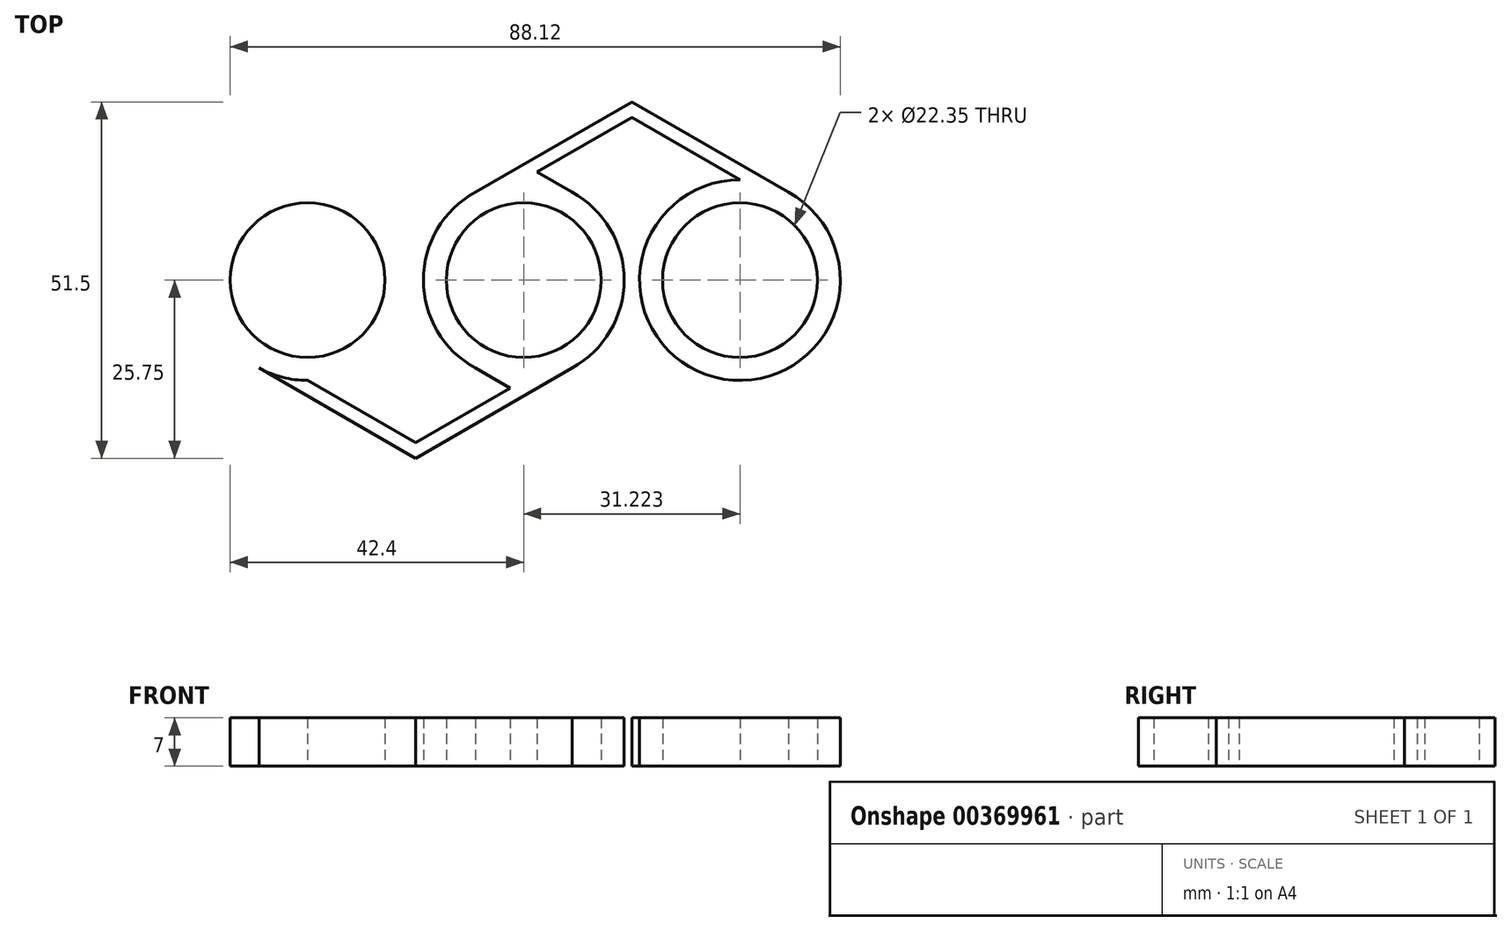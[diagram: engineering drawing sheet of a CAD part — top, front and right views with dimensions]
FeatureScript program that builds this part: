
annotation { "Feature Type Name" : "Feature", "Feature Type Description" : "" }
export const myFeature = defineFeature(function(context is Context, id is Id, definition is map)
    precondition{}
    {
        {
            var Q0;
            Q0=qCreatedBy(makeId("Top.planeOp"),FACE);
            var sketch = newSketch(context, id + "F0", { "sketchPlane" : qUnion([Q0])});
            skCircle(sketch, "E0", {"center": v(0, 0) * mm, "radius": 11.18 * mm});
            skCircle(sketch, "E1", {"center": v(0, 0) * mm, "radius": 14.5 * mm});
            skCircle(sketch, "E2", {"center": v(-31.22, 0) * mm, "radius": 11.18 * mm});
            skCircle(sketch, "E3", {"center": v(-31.22, 0) * mm, "radius": 14.5 * mm});
            skLineSegment(sketch, "E4", {"start": v(-31.22, 0) * mm, "end": v(0, 0) * mm, "construction": true});
            skLineSegment(sketch, "E5", {"start": v(-31.22, 0) * mm, "end": v(-31.22, 2) * mm, "construction": true});
            skLineSegment(sketch, "E6", {"start": v(-31.22, 0) * mm, "end": v(-31.22, -2) * mm, "construction": true});
            skLineSegment(sketch, "E7", {"start": v(0, 0) * mm, "end": v(0, 2) * mm, "construction": true});
            skLineSegment(sketch, "E8", {"start": v(0, 0) * mm, "end": v(0, -2) * mm, "construction": true});
            skLineSegment(sketch, "E9", {"start": v(-16.86, 2) * mm, "end": v(-14.36, 2) * mm});
            skLineSegment(sketch, "E10", {"start": v(-16.86, -2) * mm, "end": v(-14.36, -2) * mm});
            skLineSegment(sketch, "E11", {"start": v(-16.86, 2) * mm, "end": v(-31.22, 2) * mm, "construction": true});
            skLineSegment(sketch, "E12", {"start": v(-31.22, -2) * mm, "end": v(-16.86, -2) * mm, "construction": true});
            skLineSegment(sketch, "E13", {"start": v(-14.36, 2) * mm, "end": v(0, 2) * mm, "construction": true});
            skLineSegment(sketch, "E14", {"start": v(-14.36, -2) * mm, "end": v(0, -2) * mm, "construction": true});
            skLineSegment(sketch, "E15", {"start": v(-31.22, -2) * mm, "end": v(-31.22, -14.5) * mm, "construction": true});
            skLineSegment(sketch, "E16", {"start": v(0, -2) * mm, "end": v(0, -14.5) * mm, "construction": true});
            skLineSegment(sketch, "E17.MirrorCS", {"start": v(31.22, 0) * mm, "end": v(31.22, 2) * mm, "construction": true});
            skLineSegment(sketch, "E18.MirrorCS", {"start": v(31.22, 0) * mm, "end": v(31.22, -2) * mm, "construction": true});
            skLineSegment(sketch, "E19.MirrorCS", {"start": v(16.86, 2) * mm, "end": v(14.36, 2) * mm});
            skLineSegment(sketch, "E20.MirrorCS", {"start": v(16.86, -2) * mm, "end": v(14.36, -2) * mm});
            skLineSegment(sketch, "E21.MirrorCS", {"start": v(14.36, -2) * mm, "end": v(0, -2) * mm, "construction": true});
            skLineSegment(sketch, "E22.MirrorCS", {"start": v(31.22, -2) * mm, "end": v(31.22, -14.5) * mm, "construction": true});
            skCircle(sketch, "E23.MirrorC", {"center": v(31.22, 0) * mm, "radius": 14.5 * mm});
            skLineSegment(sketch, "E24.MirrorCS", {"start": v(31.22, 0) * mm, "end": v(0, 0) * mm, "construction": true});
            skLineSegment(sketch, "E25.MirrorCS", {"start": v(31.22, -2) * mm, "end": v(16.86, -2) * mm, "construction": true});
            skLineSegment(sketch, "E26.MirrorCS", {"start": v(16.86, 2) * mm, "end": v(31.22, 2) * mm, "construction": true});
            skCircle(sketch, "E27.MirrorC", {"center": v(31.22, 0) * mm, "radius": 11.18 * mm});
            skLineSegment(sketch, "E28.MirrorCS", {"start": v(14.36, 2) * mm, "end": v(0, 2) * mm, "construction": true});
            skLineSegment(sketch, "E29.MirrorCS", {"start": v(0, 2) * mm, "end": v(0, 14.5) * mm, "construction": true});
            skLineSegment(sketch, "E30.MirrorCS", {"start": v(-31.22, 2) * mm, "end": v(-16.86, 2) * mm, "construction": true});
            skLineSegment(sketch, "E31.MirrorCS", {"start": v(16.86, -2) * mm, "end": v(31.22, -2) * mm, "construction": true});
            skLineSegment(sketch, "E32.MirrorCS", {"start": v(-31.22, 2) * mm, "end": v(-31.22, 14.5) * mm, "construction": true});
            skLineSegment(sketch, "E33.MirrorCS", {"start": v(-16.86, -2) * mm, "end": v(-31.22, -2) * mm, "construction": true});
            skLineSegment(sketch, "E34.MirrorCS", {"start": v(31.22, 2) * mm, "end": v(16.86, 2) * mm, "construction": true});
            skLineSegment(sketch, "E35.MirrorCS", {"start": v(31.22, 2) * mm, "end": v(31.22, 14.5) * mm, "construction": true});
            skLineSegment(sketch, "E36", {"start": v(-31.22, -14.5) * mm, "end": v(0, -14.5) * mm, "construction": true});
            skLineSegment(sketch, "E37", {"start": v(-31.22, -14.5) * mm, "end": v(-15.61, -23.51) * mm});
            skPoint(sketch, "E37.endSnap0", {"position": v(-15.61, -2) * mm});
            skLineSegment(sketch, "E38", {"start": v(-15.61, -23.51) * mm, "end": v(0, -14.5) * mm});
            skLineSegment(sketch, "E39", {"start": v(-15.61, -23.51) * mm, "end": v(-15.61, -25.75) * mm});
            skLineSegment(sketch, "E40", {"start": v(-15.61, -25.75) * mm, "end": v(-38.23, -12.7) * mm});
            skLineSegment(sketch, "E41", {"start": v(-15.61, -25.75) * mm, "end": v(7, -12.7) * mm});
            skLineSegment(sketch, "E42.MirrorCS", {"start": v(15.61, -23.51) * mm, "end": v(15.61, -25.75) * mm});
            skLineSegment(sketch, "E43.MirrorCS", {"start": v(31.22, -14.5) * mm, "end": v(15.61, -23.51) * mm});
            skLineSegment(sketch, "E44.MirrorCS", {"start": v(15.61, -25.75) * mm, "end": v(38.23, -12.7) * mm});
            skLineSegment(sketch, "E45.MirrorCS", {"start": v(15.61, -23.51) * mm, "end": v(0, -14.5) * mm});
            skLineSegment(sketch, "E46.MirrorCS", {"start": v(15.61, -25.75) * mm, "end": v(-7, -12.7) * mm});
            skLineSegment(sketch, "E47.MirrorCS", {"start": v(-15.61, 23.51) * mm, "end": v(-15.61, 25.75) * mm});
            skLineSegment(sketch, "E48.MirrorCS", {"start": v(15.61, 23.51) * mm, "end": v(15.61, 25.75) * mm});
            skLineSegment(sketch, "E49.MirrorCS", {"start": v(31.22, 14.5) * mm, "end": v(15.61, 23.51) * mm});
            skLineSegment(sketch, "E50.MirrorCS", {"start": v(-15.61, 25.75) * mm, "end": v(7, 12.7) * mm});
            skLineSegment(sketch, "E51.MirrorCS", {"start": v(15.61, 23.51) * mm, "end": v(0, 14.5) * mm});
            skLineSegment(sketch, "E52.MirrorCS", {"start": v(-15.61, 23.51) * mm, "end": v(0, 14.5) * mm});
            skLineSegment(sketch, "E53.MirrorCS", {"start": v(-15.61, 25.75) * mm, "end": v(-38.23, 12.7) * mm});
            skLineSegment(sketch, "E54.MirrorCS", {"start": v(-31.22, 14.5) * mm, "end": v(-15.61, 23.51) * mm});
            skLineSegment(sketch, "E55.MirrorCS", {"start": v(15.61, 25.75) * mm, "end": v(38.23, 12.7) * mm});
            skLineSegment(sketch, "E56.MirrorCS", {"start": v(15.61, 25.75) * mm, "end": v(-7, 12.7) * mm});
            skSolve(sketch);
        }
        {
            var Q0;
            {var subQ8=sQuery(id+"F0.wireOp",EDGE,"f6e80e4f-4562-4e25-9e2e-78b92bb8b12e9.MirrorCS");Q0=makeQuery(id+"F0.imprint","IMPRINT",FACE,{"disambiguationData":[TD([[makeQuery(id+"F0.imprint","IMPRINT",EDGE,{"derivedFrom":subQ8}),1.0]])]});}
            var Q1;
            Q1=makeQuery(id+"F0.imprint","IMPRINT",FACE,{"disambiguationData":[TD([[makeQuery(id+"F0.imprint","IMPRINT",EDGE,{"derivedFrom":sQuery(id+"F0.wireOp",EDGE,"E2")}),1.0]])]});
            var Q2;
            {var subQ1=sQuery(id+"F0.wireOp",EDGE,"6nS9NaWn-jDuI-gLcJ-a9OS-xKfPHobBHDCz");Q2=makeQuery(id+"F0.imprint","IMPRINT",FACE,{"disambiguationData":[TD([[makeQuery(id+"F0.imprint","IMPRINT",EDGE,{"derivedFrom":subQ1}),1.0]])]});}
            var Q3;
            Q3=makeQuery(id+"F0.imprint","IMPRINT",FACE,{"disambiguationData":[TD([[makeQuery(id+"F0.imprint","IMPRINT",EDGE,{"derivedFrom":sQuery(id+"F0.wireOp",EDGE,"E0")}),-1.0]])]});
            var Q4;
            Q4=makeQuery(id+"F0.imprint","IMPRINT",FACE,{"disambiguationData":[TD([[makeQuery(id+"F0.imprint","IMPRINT",EDGE,{"derivedFrom":sQuery(id+"F0.wireOp",EDGE,"E27.MirrorC")}),-1.0]])]});
            var Q5;
            {var subQ3=sQuery(id+"F0.wireOp",EDGE,"f6e80e4f-4562-4e25-9e2e-78b92bb8b12e42.MirrorCS");var subQ5=sQuery(id+"F0.wireOp",EDGE,"f6e80e4f-4562-4e25-9e2e-78b92bb8b12e31.MirrorCS");var subQ6=makeQuery(id+"F0.imprint","INTERSECT",VERTEX,{"derivedFrom":[subQ5,subQ3]});Q5=makeQuery(id+"F0.imprint","IMPRINT",FACE,{"disambiguationData":[TD([[makeQuery(id+"F0.imprint","IMPRINT",EDGE,{"disambiguationData":[TD([[subQ6,1.0]])],"derivedFrom":subQ5}),-1.0]])]});}
            var Q6;
            {var subQ0=sQuery(id+"F0.wireOp",EDGE,"0d00f1c5-c491-46c6-84f9-827b81eed1ee3.MirrorCS");Q6=makeQuery(id+"F0.imprint","IMPRINT",FACE,{"disambiguationData":[TD([[makeQuery(id+"F0.imprint","IMPRINT",EDGE,{"derivedFrom":subQ0}),1.0]])]});}
            var Q7;
            {var subQ0=sQuery(id+"F0.wireOp",EDGE,"f6e80e4f-4562-4e25-9e2e-78b92bb8b12e7.MirrorCS");Q7=makeQuery(id+"F0.imprint","IMPRINT",FACE,{"disambiguationData":[TD([[makeQuery(id+"F0.imprint","IMPRINT",EDGE,{"derivedFrom":subQ0}),1.0]])]});}
            var Q8;
            {var subQ0=sQuery(id+"F0.wireOp",EDGE,"1AUodh9I-uVAc-DYUK-clBF-9MNVgow7hLd5");Q8=makeQuery(id+"F0.imprint","IMPRINT",FACE,{"disambiguationData":[TD([[makeQuery(id+"F0.imprint","IMPRINT",EDGE,{"derivedFrom":subQ0}),1.0]])]});}
            var Q9;
            {var subQ0=sQuery(id+"F0.wireOp",EDGE,"f6e80e4f-4562-4e25-9e2e-78b92bb8b12e9.MirrorCS");Q9=makeQuery(id+"F0.imprint","IMPRINT",FACE,{"disambiguationData":[TD([[makeQuery(id+"F0.imprint","IMPRINT",EDGE,{"derivedFrom":subQ0}),-1.0]])]});}
            var Q10;
            {var subQ0=sQuery(id+"F0.wireOp",EDGE,"0d00f1c5-c491-46c6-84f9-827b81eed1ee3.MirrorCS");Q10=makeQuery(id+"F0.imprint","IMPRINT",FACE,{"disambiguationData":[TD([[makeQuery(id+"F0.imprint","IMPRINT",EDGE,{"derivedFrom":subQ0}),-1.0]])]});}
            var Q11;
            {var subQ0=sQuery(id+"F0.wireOp",EDGE,"E20.MirrorCS");Q11=makeQuery(id+"F0.imprint","IMPRINT",FACE,{"disambiguationData":[TD([[makeQuery(id+"F0.imprint","IMPRINT",EDGE,{"derivedFrom":subQ0}),-1.0]])]});}
            var Q12;
            {var subQ0=sQuery(id+"F0.wireOp",EDGE,"E10");Q12=makeQuery(id+"F0.imprint","IMPRINT",FACE,{"disambiguationData":[TD([[makeQuery(id+"F0.imprint","IMPRINT",EDGE,{"derivedFrom":subQ0}),1.0]])]});}
            var Q13;
            {var subQ0=sQuery(id+"F0.wireOp",EDGE,"f6e80e4f-4562-4e25-9e2e-78b92bb8b12e11.MirrorCS");Q13=makeQuery(id+"F0.imprint","IMPRINT",FACE,{"disambiguationData":[TD([[makeQuery(id+"F0.imprint","IMPRINT",EDGE,{"derivedFrom":subQ0}),-1.0]])]});}
            var Q14;
            {var subQ0=sQuery(id+"F0.wireOp",EDGE,"f6e80e4f-4562-4e25-9e2e-78b92bb8b12e7.MirrorCS");Q14=makeQuery(id+"F0.imprint","IMPRINT",FACE,{"disambiguationData":[TD([[makeQuery(id+"F0.imprint","IMPRINT",EDGE,{"derivedFrom":subQ0}),-1.0]])]});}
            var Q15;
            {var subQ0=sQuery(id+"F0.wireOp",EDGE,"1AUodh9I-uVAc-DYUK-clBF-9MNVgow7hLd5");Q15=makeQuery(id+"F0.imprint","IMPRINT",FACE,{"disambiguationData":[TD([[makeQuery(id+"F0.imprint","IMPRINT",EDGE,{"derivedFrom":subQ0}),-1.0]])]});}
            var Q16;
            {var subQ0=sQuery(id+"F0.wireOp",EDGE,"f6e80e4f-4562-4e25-9e2e-78b92bb8b12e11.MirrorCS");Q16=makeQuery(id+"F0.imprint","IMPRINT",FACE,{"disambiguationData":[TD([[makeQuery(id+"F0.imprint","IMPRINT",EDGE,{"derivedFrom":subQ0}),1.0]])]});}
            var Q17;
            {var subQ3=sQuery(id+"F0.wireOp",EDGE,"E177.MirrorCS");var subQ5=sQuery(id+"F0.wireOp",EDGE,"ElZhDbfO-O3BU-QykL-sw9T-ieMVL2Ok5VLO");var subQ7=makeQuery(id+"F0.imprint","INTERSECT",VERTEX,{"derivedFrom":[subQ5,subQ3]});Q17=makeQuery(id+"F0.imprint","IMPRINT",FACE,{"disambiguationData":[TD([[makeQuery(id+"F0.imprint","IMPRINT",EDGE,{"disambiguationData":[TD([[subQ7,1.0]])],"derivedFrom":subQ5}),-1.0]])]});}
            var Q18;
            {var subQ0=sQuery(id+"F0.wireOp",EDGE,"kMkZqgJF-6WJB-tFxM-xSpB-YcTjBLjsbUN4");Q18=makeQuery(id+"F0.imprint","IMPRINT",FACE,{"disambiguationData":[TD([[makeQuery(id+"F0.imprint","IMPRINT",EDGE,{"derivedFrom":subQ0}),-1.0]])]});}
            var Q19;
            {var subQ1=sQuery(id+"F0.wireOp",EDGE,"E1");var subQ3=sQuery(id+"F0.wireOp",EDGE,"E41");var subQ4=makeQuery(id+"F0.imprint","INTERSECT",VERTEX,{"derivedFrom":[subQ1,subQ3]});Q19=makeQuery(id+"F0.imprint","IMPRINT",FACE,{"disambiguationData":[TD([[makeQuery(id+"F0.imprint","IMPRINT",EDGE,{"disambiguationData":[TD([[subQ4,1.0]])],"derivedFrom":subQ3}),1.0]])]});}
            var Q20;
            {var subQ3=sQuery(id+"F0.wireOp",EDGE,"E46.MirrorCS");var subQ5=sQuery(id+"F0.wireOp",EDGE,"E41");var subQ7=makeQuery(id+"F0.imprint","INTERSECT",VERTEX,{"derivedFrom":[subQ5,subQ3]});Q20=makeQuery(id+"F0.imprint","IMPRINT",FACE,{"disambiguationData":[TD([[makeQuery(id+"F0.imprint","IMPRINT",EDGE,{"disambiguationData":[TD([[subQ7,-1.0]])],"derivedFrom":subQ5}),1.0]])]});}
            var Q21;
            {var subQ0=sQuery(id+"F0.wireOp",EDGE,"E39");Q21=makeQuery(id+"F0.imprint","IMPRINT",FACE,{"disambiguationData":[TD([[makeQuery(id+"F0.imprint","IMPRINT",EDGE,{"derivedFrom":subQ0}),1.0]])]});}
            var Q22;
            {var subQ1=sQuery(id+"F0.wireOp",EDGE,"E1");var subQ3=sQuery(id+"F0.wireOp",EDGE,"E46.MirrorCS");var subQ4=makeQuery(id+"F0.imprint","INTERSECT",VERTEX,{"derivedFrom":[subQ1,subQ3]});Q22=makeQuery(id+"F0.imprint","IMPRINT",FACE,{"disambiguationData":[TD([[makeQuery(id+"F0.imprint","IMPRINT",EDGE,{"disambiguationData":[TD([[subQ4,1.0]])],"derivedFrom":subQ3}),-1.0]])]});}
            var Q23;
            {var subQ0=sQuery(id+"F0.wireOp",EDGE,"E37");Q23=makeQuery(id+"F0.imprint","IMPRINT",FACE,{"disambiguationData":[TD([[makeQuery(id+"F0.imprint","IMPRINT",EDGE,{"derivedFrom":subQ0}),-1.0]])]});}
            var Q24;
            {var subQ0=sQuery(id+"F0.wireOp",EDGE,"E56.MirrorCS");var subQ1=sQuery(id+"F0.wireOp",EDGE,"E50.MirrorCS");var subQ2=makeQuery(id+"F0.imprint","INTERSECT",VERTEX,{"derivedFrom":[subQ1,subQ0]});Q24=makeQuery(id+"F0.imprint","IMPRINT",FACE,{"disambiguationData":[TD([[makeQuery(id+"F0.imprint","IMPRINT",EDGE,{"disambiguationData":[TD([[subQ2,-1.0]])],"derivedFrom":subQ1}),-1.0]])]});}
            var Q25;
            {var subQ0=sQuery(id+"F0.wireOp",EDGE,"E50.MirrorCS");var subQ1=sQuery(id+"F0.wireOp",EDGE,"E1");var subQ2=makeQuery(id+"F0.imprint","INTERSECT",VERTEX,{"derivedFrom":[subQ1,subQ0]});Q25=makeQuery(id+"F0.imprint","IMPRINT",FACE,{"disambiguationData":[TD([[makeQuery(id+"F0.imprint","IMPRINT",EDGE,{"disambiguationData":[TD([[subQ2,1.0]])],"derivedFrom":subQ0}),-1.0]])]});}
            var Q26;
            {var subQ1=sQuery(id+"F0.wireOp",EDGE,"E1");var subQ3=sQuery(id+"F0.wireOp",EDGE,"E56.MirrorCS");var subQ4=makeQuery(id+"F0.imprint","INTERSECT",VERTEX,{"derivedFrom":[subQ1,subQ3]});Q26=makeQuery(id+"F0.imprint","IMPRINT",FACE,{"disambiguationData":[TD([[makeQuery(id+"F0.imprint","IMPRINT",EDGE,{"disambiguationData":[TD([[subQ4,1.0]])],"derivedFrom":subQ3}),1.0]])]});}
            var Q27;
            {var subQ0=sQuery(id+"F0.wireOp",EDGE,"E48.MirrorCS");Q27=makeQuery(id+"F0.imprint","IMPRINT",FACE,{"disambiguationData":[TD([[makeQuery(id+"F0.imprint","IMPRINT",EDGE,{"derivedFrom":subQ0}),1.0]])]});}
            var Q28;
            Q28=makeQuery(id+"F0.imprint","IMPRINT",FACE,{"disambiguationData":[TD([[makeQuery(id+"F0.imprint","IMPRINT",EDGE,{"derivedFrom":sQuery(id+"F0.wireOp",EDGE,"E48.MirrorCS")}),-1.0]])]});
            extrude(context, id + "F1", {"entities" : qUnion([Q0, Q1, Q2, Q3, Q4, Q5, Q6, Q7, Q8, Q9, Q10, Q11, Q12, Q13, Q14, Q15, Q16, Q17, Q18, Q19, Q20, Q21, Q22, Q23, Q24, Q25, Q26, Q27, Q28]), "depth" : 7 * mm, "offsetDistance" : 25 * mm});
        }
    });
